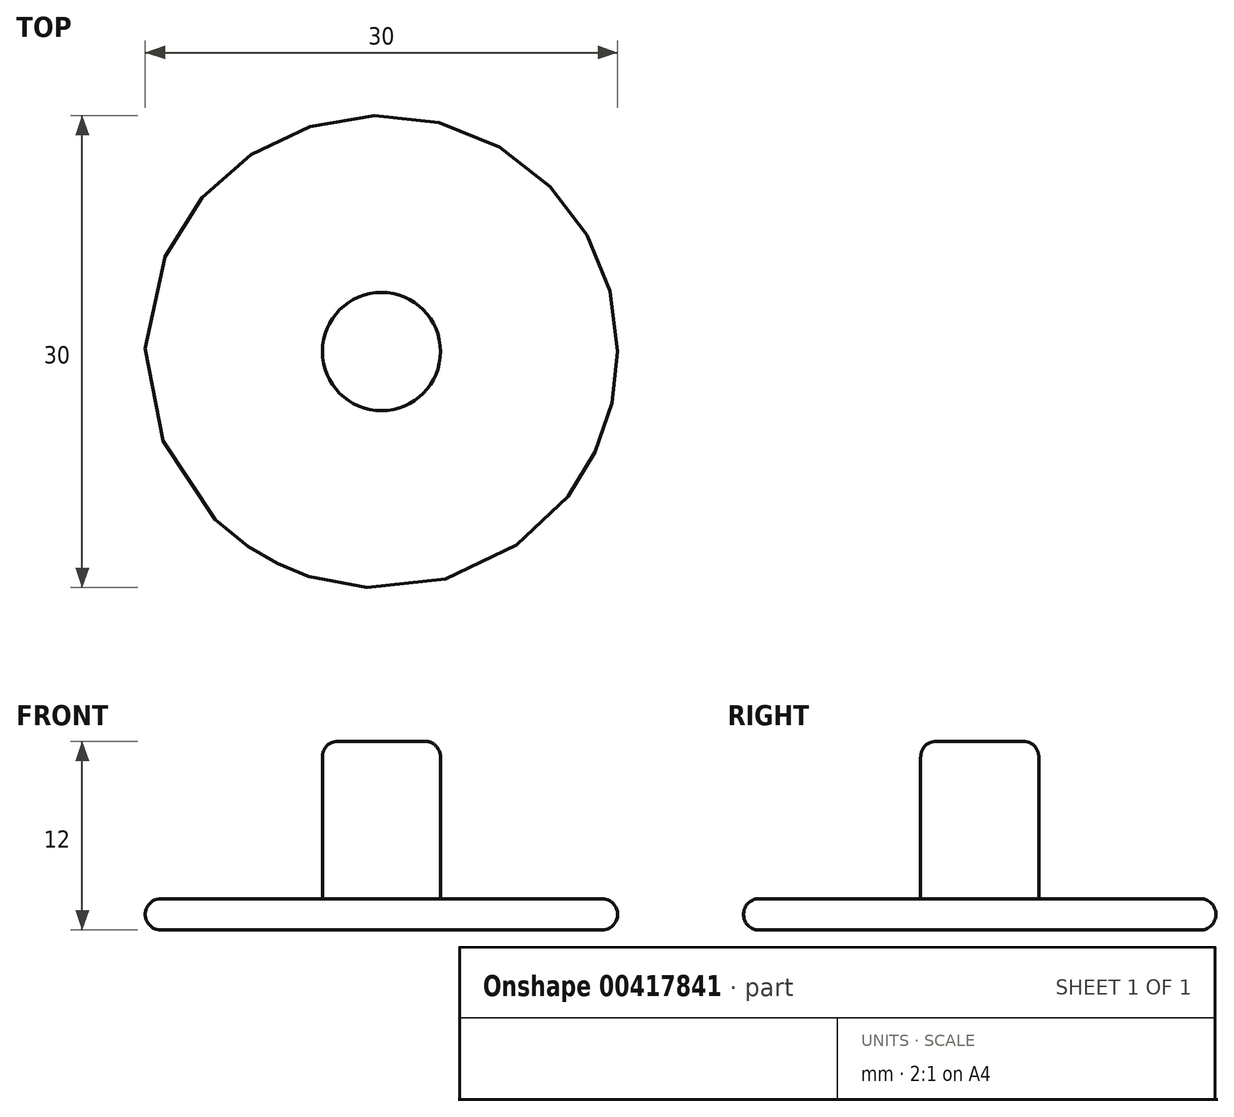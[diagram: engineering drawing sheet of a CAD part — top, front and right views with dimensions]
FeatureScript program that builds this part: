
annotation { "Feature Type Name" : "Feature", "Feature Type Description" : "" }
export const myFeature = defineFeature(function(context is Context, id is Id, definition is map)
    precondition{}
    {
        {
            var Q0;
            Q0=qCreatedBy(makeId("Top.planeOp"),FACE);
            var sketch = newSketch(context, id + "F0", { "sketchPlane" : qUnion([Q0])});
            skCircle(sketch, "E0", {"center": v(0, 0) * mm, "radius": 15 * mm});
            skSolve(sketch);
        }
        {
            var Q0;
            Q0 = qSketchRegion(id + "F0", true);
            extrude(context, id + "F1", {"entities" : qUnion([Q0]), "depth" : 2 * mm});
        }
        {
            var Q0;
            Q0=makeQuery(id+"F1.opExtrude","CAP_FACE",FACE,{"disambiguationData":[OSD([sQuery(id+"F0.wireOp",EDGE,"E0")])],"isStart":false});
            var sketch = newSketch(context, id + "F2", { "sketchPlane" : qUnion([Q0])});
            skCircle(sketch, "E1", {"center": v(0, 0) * mm, "radius": 3.75 * mm});
            skSolve(sketch);
        }
        {
            var Q0;
            Q0 = qSketchRegion(id + "F2", true);
            extrude(context, id + "F3", {"entities" : qUnion([Q0]), "operationType" : NewBodyOperationType.ADD, "depth" : 10 * mm});
        }
        {
            var Q0;
            Q0=makeQuery(id+"F3.opExtrude","CAP_FACE",FACE,{"disambiguationData":[OSD([sQuery(id+"F2.wireOp",EDGE,"E1")])],"isStart":false});
            var Q1;
            Q1=makeQuery(id+"F1.opExtrude","SWEPT_FACE",FACE,{"disambiguationData":[OSD([sQuery(id+"F0.wireOp",EDGE,"E0")])]});
            fillet(context, id + "F4", {"entities" : qUnion([Q0, Q1]), "radius" : 1 * mm, "tangentPropagation" : true, "allowEdgeOverflow" : false});
        }
    });
